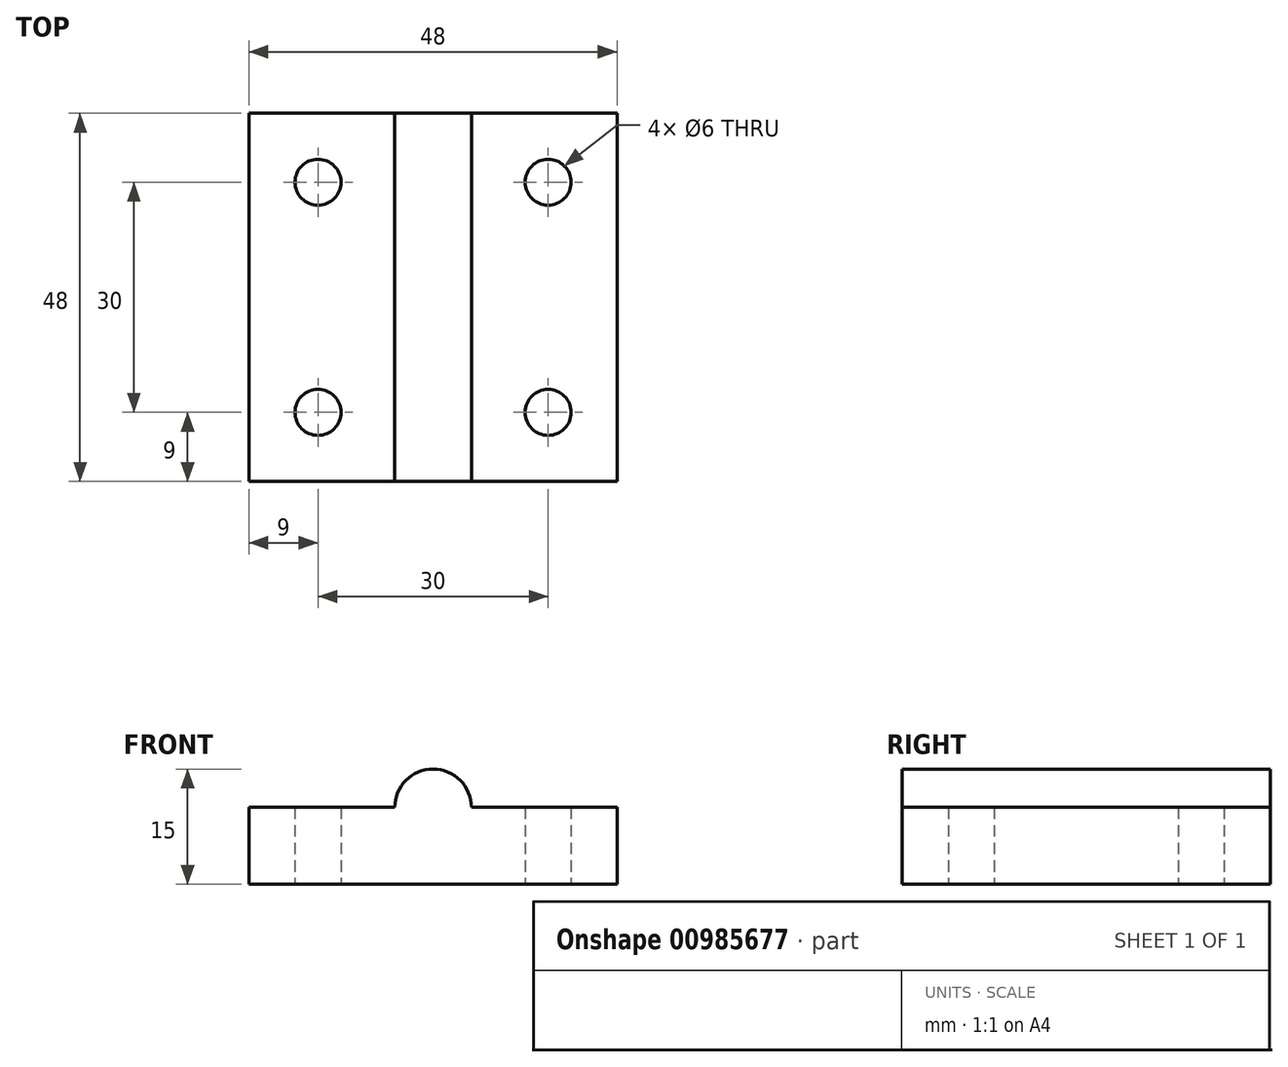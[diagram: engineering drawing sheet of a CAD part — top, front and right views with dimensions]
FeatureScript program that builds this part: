
annotation { "Feature Type Name" : "Feature", "Feature Type Description" : "" }
export const myFeature = defineFeature(function(context is Context, id is Id, definition is map)
    precondition{}
    {
        {
            var Q0;
            Q0=qCreatedBy(makeId("Top.planeOp"),FACE);
            var sketch = newSketch(context, id + "F0", { "sketchPlane" : qUnion([Q0])});
            skLineSegment(sketch, "E0.bottom", {"start": v(0, 0) * mm, "end": v(48, 0) * mm});
            skLineSegment(sketch, "E0.top", {"start": v(0, 48) * mm, "end": v(48, 48) * mm});
            skLineSegment(sketch, "E0.left", {"start": v(0, 0) * mm, "end": v(0, 48) * mm});
            skLineSegment(sketch, "E0.right", {"start": v(48, 0) * mm, "end": v(48, 48) * mm});
            skSolve(sketch);
        }
        {
            var Q0;
            Q0=makeQuery(id+"F0.imprint","IMPRINT",FACE,{"disambiguationData":[TD([[makeQuery(id+"F0.imprint","IMPRINT",EDGE,{"derivedFrom":sQuery(id+"F0.wireOp",EDGE,"E0.bottom")}),1.0]])]});
            extrude(context, id + "F1", {"entities" : qUnion([Q0]), "depth" : 10 * mm, "offsetDistance" : 25 * mm});
        }
        {
            var Q0;
            Q0=makeQuery(id+"F1.opExtrude","SWEPT_FACE",FACE,{"disambiguationData":[OSD([sQuery(id+"F0.wireOp",EDGE,"E0.bottom")])]});
            var sketch = newSketch(context, id + "F2", { "sketchPlane" : qUnion([Q0])});
            skCircle(sketch, "E1", {"center": v(24, 10) * mm, "radius": 5 * mm});
            skSolve(sketch);
        }
        {
            var Q0;
            {var subQ0=sQuery(id+"F2.wireOp",EDGE,"E1");var subQ1=makeQuery(id+"F1.opExtrude","CAP_EDGE",EDGE,{"disambiguationData":[OSD([sQuery(id+"F0.wireOp",EDGE,"E0.bottom")])],"isStart":false});var subQ2=makeQuery(id+"F2.imprint","INTERSECT",VERTEX,{"disambiguationData":[OD(0.0)],"derivedFrom":[subQ1,subQ0]});Q0=makeQuery(id+"F2.imprint","IMPRINT",FACE,{"disambiguationData":[TD([[makeQuery(id+"F2.imprint","IMPRINT",EDGE,{"disambiguationData":[TD([[subQ2,1.0]])],"derivedFrom":subQ0}),1.0]])]});}
            var Q1;
            Q1=makeQuery(id+"F1.opExtrude","SWEPT_FACE",FACE,{"disambiguationData":[OSD([sQuery(id+"F0.wireOp",EDGE,"E0.top")])]});
            extrude(context, id + "F3", {"entities" : qUnion([Q0]), "operationType" : NewBodyOperationType.ADD, "endBound" : BoundingType.UP_TO_SURFACE, "oppositeDirection" : true, "depth" : 25 * mm, "endBoundEntityFace" : qUnion([Q1]), "offsetDistance" : 25 * mm});
        }
        {
            var Q0;
            Q0=makeQuery(id+"F1.opExtrude","CAP_FACE",FACE,{"disambiguationData":[OSD([sQuery(id+"F0.wireOp",EDGE,"E0.bottom"),sQuery(id+"F0.wireOp",EDGE,"E0.top"),sQuery(id+"F0.wireOp",EDGE,"E0.left"),sQuery(id+"F0.wireOp",EDGE,"E0.right")])],"isStart":true});
            var sketch = newSketch(context, id + "F4", { "sketchPlane" : qUnion([Q0])});
            skLineSegment(sketch, "E2", {"start": v(0, 0) * mm, "end": v(48, -48) * mm, "construction": true});
            skLineSegment(sketch, "E3", {"start": v(0, -48) * mm, "end": v(48, 0) * mm, "construction": true});
            skLineSegment(sketch, "E4.bottom", {"start": v(39, -9) * mm, "end": v(9, -9) * mm, "construction": true});
            skLineSegment(sketch, "E4.top", {"start": v(39, -39) * mm, "end": v(9, -39) * mm, "construction": true});
            skLineSegment(sketch, "E4.left", {"start": v(39, -9) * mm, "end": v(39, -39) * mm, "construction": true});
            skLineSegment(sketch, "E4.right", {"start": v(9, -9) * mm, "end": v(9, -39) * mm, "construction": true});
            skPoint(sketch, "E4.middle", {"position": v(24, -24) * mm});
            skSolve(sketch);
        }
        {
            var Q0;
            Q0=sQuery(id+"F4.wireOp",VERTEX,"E4.bottom.end");
            var Q1;
            Q1=sQuery(id+"F4.wireOp",VERTEX,"E4.top.end");
            var Q2;
            Q2=sQuery(id+"F4.wireOp",VERTEX,"E4.top.start");
            var Q3;
            Q3=sQuery(id+"F4.wireOp",VERTEX,"E4.bottom.start");
            var Q4;
            Q4=makeQuery(id+"F1.opExtrude","SWEPT_BODY",BODY,{"disambiguationData":[OSD([sQuery(id+"F0.wireOp",EDGE,"E0.bottom"),sQuery(id+"F0.wireOp",EDGE,"E0.top"),sQuery(id+"F0.wireOp",EDGE,"E0.left"),sQuery(id+"F0.wireOp",EDGE,"E0.right")])]});
            hole(context, id + "F5", {"style" : HoleStyle.SIMPLE, "endStyle" : HoleEndStyle.THROUGH, "holeDiameter" : 6 * mm, "majorDiameter" : 5 * mm, "isTappedThrough" : true, "tappedDepth" : 12 * mm, "tapClearance" : 3, "startFromSketch" : true, "locations" : qUnion([Q0, Q1, Q2, Q3]), "scope" : qUnion([Q4])});
        }
    });
